# Revit family: 81MEJC-81MGJC-81MFJC-81MHJC_MC Chair_Mesh Seat Mesh Pad Back No Armrest Silver Frame Black Shell_1
name_source: partatom
category: Furniture
revit_build: Autodesk Revit 2017 (Build: 20160225_1515(x64)
units: mm (PartAtom-declared; Revit-internal decimal feet)

## family parameters
Always vertical = Yes
Cut with Voids When Loaded = No
OmniClass Number = 23.40.20.00
OmniClass Title = General Furniture and Specialties
Room Calculation Point = No
Shared = No
Work Plane-Based = No

## types (48) — shared parameters
Assembly Code = E2020200
Caster = okm_G155
D = 580 mm  [stored 1.90289 ft]
Frame = okm_silver FX4
H = 850 mm  [stored 2.78871 ft]
Keynote = 12490
Kind = Chair
Manufacturer = Okamura Corporation
Product Categories = Multi-Purpose Chair
Shell = okm_G721
URL = http://www.okamura.co.jp
W = 596 mm  [stored 1.95538 ft]

## per-type parameters (varying)
| type | Back | Product Number | Seat |
| F1E2（White）_Without Brake Hard Caster | okm_F1A2 | 81MEJC | okm_F1C2 |
| F1E7（Beige）_Without Brake Hard Caster | okm_F1A7 | 81MEJC | okm_F1C7 |
| F1E8（Dark Brown）_Without Brake Hard Caster | okm_F1A8 | 81MEJC | okm_F1C8 |
| F1E3（Light Gray）_Without Brake Hard Caster | okm_F1A3 | 81MEJC | okm_F1C3 |
| F1F2（Medium Gray）_Without Brake Hard Caster | okm_F1B2 | 81MEJC | okm_F1D2 |
| F1E1（Black）_Without Brake Hard Caster | okm_F1A1 | 81MEJC | okm_F1C1 |
| F1E0（Purple）_Without Brake Hard Caster | okm_F1A0 | 81MEJC | okm_F1C0 |
| F1E4（Dark Blue）_Without Brake Hard Caster | okm_F1A4 | 81MEJC | okm_F1C4 |
| F1E6（Sage）_Without Brake Hard Caster | okm_F1A6 | 81MEJC | okm_F1C6 |
| F1F5（Dark Green）_Without Brake Hard Caster | okm_F1B5 | 81MEJC | okm_F1D5 |
| F1F8（Orange Red）_Without Brake Hard Caster | okm_F1B8 | 81MEJC | okm_F1D8 |
| F1E9（Red）_Without Brake Hard Caster | okm_F1A9 | 81MEJC | okm_F1C9 |
| F1E2（White）_With Brake Hard Caster | okm_F1A2 | 81MFJC | okm_F1C2 |
| F1E7（Beige）_With Brake Hard Caster | okm_F1A7 | 81MFJC | okm_F1C7 |
| F1E8（Dark Brown）_With Brake Hard Caster | okm_F1A8 | 81MFJC | okm_F1C8 |
| F1E3（Light Gray）_With Brake Hard Caster | okm_F1A3 | 81MFJC | okm_F1C3 |
| F1F2（Medium Gray）_With Brake Hard Caster | okm_F1B2 | 81MFJC | okm_F1D2 |
| F1E1（Black）_With Brake Hard Caster | okm_F1A1 | 81MFJC | okm_F1C1 |
| F1E0（Purple）_With Brake Hard Caster | okm_F1A0 | 81MFJC | okm_F1C0 |
| F1E4（Dark Blue）_With Brake Hard Caster | okm_F1A4 | 81MFJC | okm_F1C4 |
| F1E6（Sage）_With Brake Hard Caster | okm_F1A6 | 81MFJC | okm_F1C6 |
| F1F5（Dark Green）_With Brake Hard Caster | okm_F1B5 | 81MFJC | okm_F1D5 |
| F1F8（Orange Red）_With Brake Hard Caster | okm_F1B8 | 81MFJC | okm_F1D8 |
| F1E9（Red）_With Brake Hard Caster | okm_F1A9 | 81MFJC | okm_F1C9 |
| F1E2（White）_Without Brake Soft Caster | okm_F1A2 | 81MGJC | okm_F1C2 |
| F1E7（Beige）_Without Brake Soft Caster | okm_F1A7 | 81MGJC | okm_F1C7 |
| F1E8（Dark Brown）_Without Brake Soft Caster | okm_F1A8 | 81MGJC | okm_F1C8 |
| F1E3（Light Gray）_Without Brake Soft Caster | okm_F1A3 | 81MGJC | okm_F1C3 |
| F1F2（Medium Gray）_Without Brake Soft Caster | okm_F1B2 | 81MGJC | okm_F1D2 |
| F1E1（Black）_Without Brake Soft Caster | okm_F1A1 | 81MGJC | okm_F1C1 |
| F1E0（Purple）_Without Brake Soft Caster | okm_F1A0 | 81MGJC | okm_F1C0 |
| F1E4（Dark Blue）_Without Brake Soft Caster | okm_F1A4 | 81MGJC | okm_F1C4 |
| F1E6（Sage）_Without Brake Soft Caster | okm_F1A6 | 81MGJC | okm_F1C6 |
| F1F5（Dark Green）_Without Brake Soft Caster | okm_F1B5 | 81MGJC | okm_F1D5 |
| F1F8（Orange Red）_Without Brake Soft Caster | okm_F1B8 | 81MGJC | okm_F1D8 |
| F1E9（Red）_Without Brake Soft Caster | okm_F1A9 | 81MGJC | okm_F1C9 |
| F1E2（White）_With Brake Soft Caster | okm_F1A2 | 81MHJC | okm_F1C2 |
| F1E7（Beige）_With Brake Soft Caster | okm_F1A7 | 81MHJC | okm_F1C7 |
| F1E8（Dark Brown）_With Brake Soft Caster | okm_F1A8 | 81MHJC | okm_F1C8 |
| F1E3（Light Gray）_With Brake Soft Caster | okm_F1A3 | 81MHJC | okm_F1C3 |
| F1F2（Medium Gray）_With Brake Soft Caster | okm_F1B2 | 81MHJC | okm_F1D2 |
| F1E1（Black）_With Brake Soft Caster | okm_F1A1 | 81MHJC | okm_F1C1 |
| F1E0（Purple）_With Brake Soft Caster | okm_F1A0 | 81MHJC | okm_F1C0 |
| F1E4（Dark Blue）_With Brake Soft Caster | okm_F1A4 | 81MHJC | okm_F1C4 |
| F1E6（Sage）_With Brake Soft Caster | okm_F1A6 | 81MHJC | okm_F1C6 |
| F1F5（Dark Green）_With Brake Soft Caster | okm_F1B5 | 81MHJC | okm_F1D5 |
| F1F8（Orange Red）_With Brake Soft Caster | okm_F1B8 | 81MHJC | okm_F1D8 |
| F1E9（Red）_With Brake Soft Caster | okm_F1A9 | 81MHJC | okm_F1C9 |

note: [stored X ft] marks values corroborated as IEEE doubles in the binary element streams (Revit-internal decimal feet)
